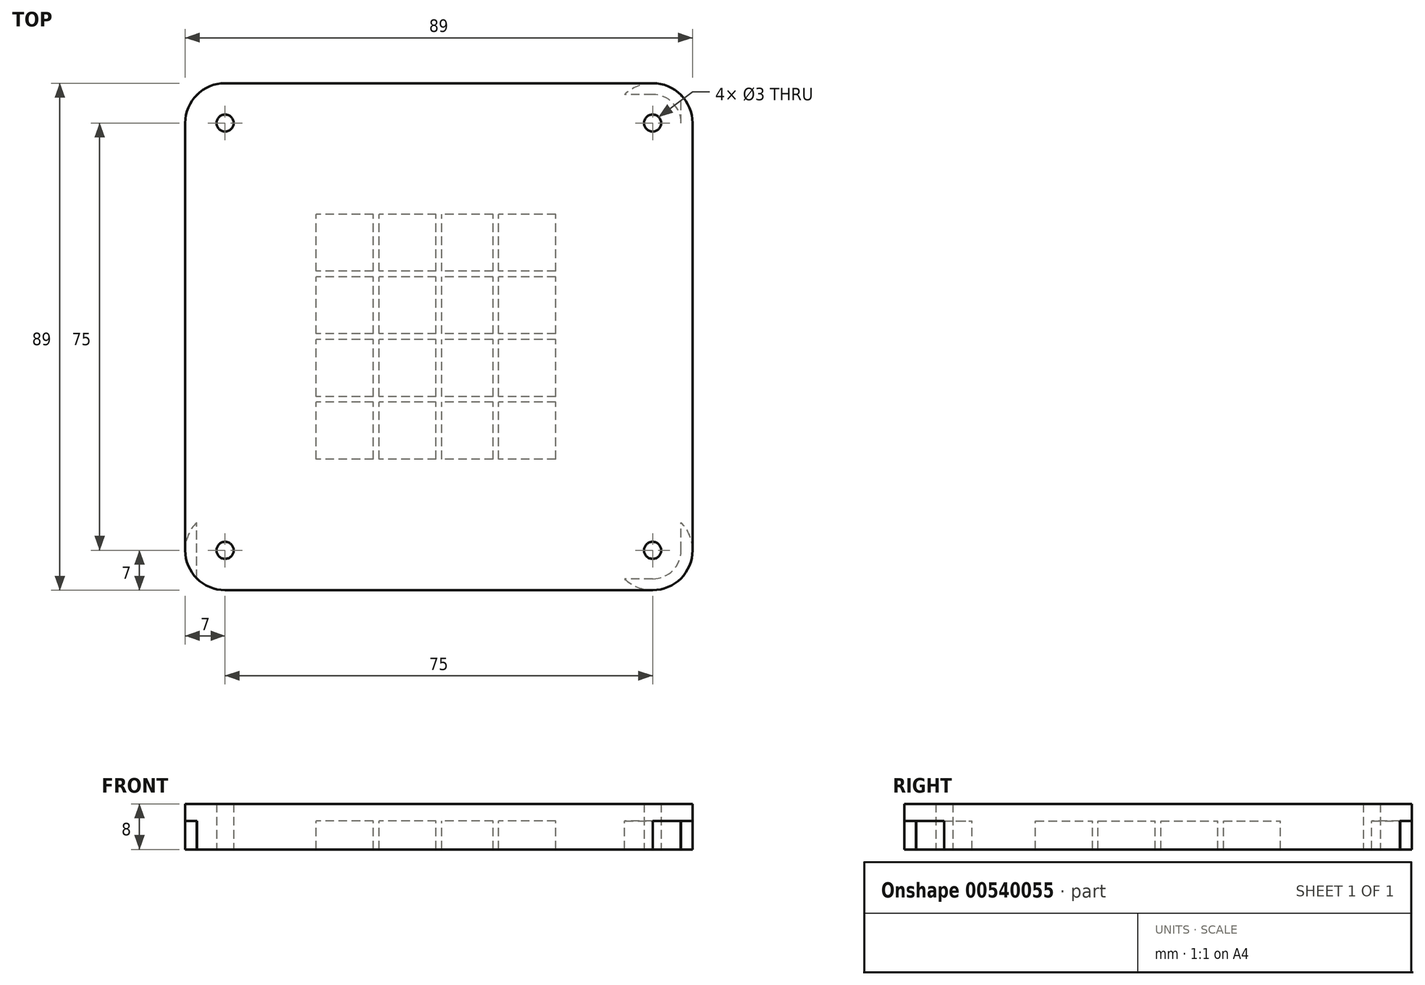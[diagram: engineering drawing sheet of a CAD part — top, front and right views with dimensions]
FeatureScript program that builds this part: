
annotation { "Feature Type Name" : "Feature", "Feature Type Description" : "" }
export const myFeature = defineFeature(function(context is Context, id is Id, definition is map)
    precondition{}
    {
        {
            var Q0;
            Q0=qCreatedBy(makeId("Top.planeOp"),FACE);
            var sketch = newSketch(context, id + "F0", { "sketchPlane" : qUnion([Q0])});
            skLineSegment(sketch, "E0.bottom", {"start": v(37.5, 37.5) * mm, "end": v(-37.5, 37.5) * mm});
            skLineSegment(sketch, "E0.top", {"start": v(37.5, -37.5) * mm, "end": v(-37.5, -37.5) * mm});
            skLineSegment(sketch, "E0.left", {"start": v(37.5, 37.5) * mm, "end": v(37.5, -37.5) * mm});
            skLineSegment(sketch, "E0.right", {"start": v(-37.5, 37.5) * mm, "end": v(-37.5, -37.5) * mm});
            skPoint(sketch, "E0.middle", {"position": v(0, 0) * mm});
            skLineSegment(sketch, "E1.bottom", {"start": v(44.5, 44.5) * mm, "end": v(-44.5, 44.5) * mm});
            skLineSegment(sketch, "E1.top", {"start": v(44.5, -44.5) * mm, "end": v(-44.5, -44.5) * mm});
            skLineSegment(sketch, "E1.left", {"start": v(44.5, 44.5) * mm, "end": v(44.5, -44.5) * mm});
            skLineSegment(sketch, "E1.right", {"start": v(-44.5, 44.5) * mm, "end": v(-44.5, -44.5) * mm});
            skCircle(sketch, "E2", {"center": v(37.5, 37.5) * mm, "radius": 7 * mm});
            skCircle(sketch, "E3", {"center": v(-37.5, 37.5) * mm, "radius": 7 * mm});
            skCircle(sketch, "E4", {"center": v(-37.5, -37.5) * mm, "radius": 7 * mm});
            skCircle(sketch, "E5", {"center": v(37.5, -37.5) * mm, "radius": 7 * mm});
            skCircle(sketch, "E6", {"center": v(-37.5, 37.5) * mm, "radius": 1.5 * mm});
            skCircle(sketch, "E7", {"center": v(37.5, 37.5) * mm, "radius": 1.5 * mm});
            skCircle(sketch, "E8", {"center": v(37.5, -37.5) * mm, "radius": 1.5 * mm});
            skCircle(sketch, "E9", {"center": v(-37.5, -37.5) * mm, "radius": 1.5 * mm});
            skSolve(sketch);
        }
        {
            var Q0;
            {var subQ0=sQuery(id+"F0.wireOp",EDGE,"E2");var subQ1=sQuery(id+"F0.wireOp",EDGE,"E0.bottom");var subQ2=makeQuery(id+"F0.imprint","INTERSECT",VERTEX,{"derivedFrom":[subQ1,subQ0]});Q0=makeQuery(id+"F0.imprint","IMPRINT",FACE,{"disambiguationData":[TD([[makeQuery(id+"F0.imprint","IMPRINT",EDGE,{"disambiguationData":[TD([[subQ2,-1.0]])],"derivedFrom":subQ1}),-1.0]])]});}
            var Q1;
            {var subQ0=sQuery(id+"F0.wireOp",EDGE,"E5");var subQ1=sQuery(id+"F0.wireOp",EDGE,"E0.top");var subQ2=makeQuery(id+"F0.imprint","INTERSECT",VERTEX,{"derivedFrom":[subQ1,subQ0]});Q1=makeQuery(id+"F0.imprint","IMPRINT",FACE,{"disambiguationData":[TD([[makeQuery(id+"F0.imprint","IMPRINT",EDGE,{"disambiguationData":[TD([[subQ2,-1.0]])],"derivedFrom":subQ1}),1.0]])]});}
            var Q2;
            {var subQ0=sQuery(id+"F0.wireOp",EDGE,"E2");var subQ1=sQuery(id+"F0.wireOp",EDGE,"E0.left");var subQ2=makeQuery(id+"F0.imprint","INTERSECT",VERTEX,{"derivedFrom":[subQ1,subQ0]});Q2=makeQuery(id+"F0.imprint","IMPRINT",FACE,{"disambiguationData":[TD([[makeQuery(id+"F0.imprint","IMPRINT",EDGE,{"disambiguationData":[TD([[subQ2,-1.0]])],"derivedFrom":subQ1}),1.0]])]});}
            var Q3;
            {var subQ0=sQuery(id+"F0.wireOp",EDGE,"E3");var subQ1=sQuery(id+"F0.wireOp",EDGE,"E0.right");var subQ2=makeQuery(id+"F0.imprint","INTERSECT",VERTEX,{"derivedFrom":[subQ1,subQ0]});Q3=makeQuery(id+"F0.imprint","IMPRINT",FACE,{"disambiguationData":[TD([[makeQuery(id+"F0.imprint","IMPRINT",EDGE,{"disambiguationData":[TD([[subQ2,-1.0]])],"derivedFrom":subQ1}),-1.0]])]});}
            var Q4;
            {var subQ2=sQuery(id+"F0.wireOp",EDGE,"E0.bottom");var subQ4=sQuery(id+"F0.wireOp",EDGE,"E7");var subQ9=makeQuery(id+"F0.imprint","INTERSECT",VERTEX,{"derivedFrom":[subQ2,subQ4]});Q4=makeQuery(id+"F0.imprint","IMPRINT",FACE,{"disambiguationData":[TD([[makeQuery(id+"F0.imprint","IMPRINT",EDGE,{"disambiguationData":[TD([[subQ9,-1.0]])],"derivedFrom":subQ2}),-1.0]])]});}
            var Q5;
            {var subQ0=sQuery(id+"F0.wireOp",EDGE,"E3");var subQ4=sQuery(id+"F0.wireOp",EDGE,"E0.bottom");var subQ8=makeQuery(id+"F0.imprint","INTERSECT",VERTEX,{"derivedFrom":[subQ4,subQ0]});Q5=makeQuery(id+"F0.imprint","IMPRINT",FACE,{"disambiguationData":[TD([[makeQuery(id+"F0.imprint","IMPRINT",EDGE,{"disambiguationData":[TD([[subQ8,-1.0]])],"derivedFrom":subQ4}),-1.0]])]});}
            var Q6;
            {var subQ4=sQuery(id+"F0.wireOp",EDGE,"E8");var subQ7=sQuery(id+"F0.wireOp",EDGE,"E0.top");var subQ9=makeQuery(id+"F0.imprint","INTERSECT",VERTEX,{"derivedFrom":[subQ7,subQ4]});Q6=makeQuery(id+"F0.imprint","IMPRINT",FACE,{"disambiguationData":[TD([[makeQuery(id+"F0.imprint","IMPRINT",EDGE,{"disambiguationData":[TD([[subQ9,-1.0]])],"derivedFrom":subQ7}),1.0]])]});}
            var Q7;
            {var subQ0=sQuery(id+"F0.wireOp",EDGE,"E4");var subQ5=sQuery(id+"F0.wireOp",EDGE,"E0.top");var subQ6=makeQuery(id+"F0.imprint","INTERSECT",VERTEX,{"derivedFrom":[subQ5,subQ0]});Q7=makeQuery(id+"F0.imprint","IMPRINT",FACE,{"disambiguationData":[TD([[makeQuery(id+"F0.imprint","IMPRINT",EDGE,{"disambiguationData":[TD([[subQ6,-1.0]])],"derivedFrom":subQ5}),1.0]])]});}
            var Q8;
            {var subQ5=sQuery(id+"F0.wireOp",EDGE,"E0.bottom");var subQ7=sQuery(id+"F0.wireOp",EDGE,"E2");var subQ12=makeQuery(id+"F0.imprint","INTERSECT",VERTEX,{"derivedFrom":[subQ5,subQ7]});Q8=makeQuery(id+"F0.imprint","IMPRINT",FACE,{"disambiguationData":[TD([[makeQuery(id+"F0.imprint","IMPRINT",EDGE,{"disambiguationData":[TD([[subQ12,-1.0]])],"derivedFrom":subQ5}),1.0]])]});}
            var Q9;
            {var subQ0=sQuery(id+"F0.wireOp",EDGE,"E3");var subQ1=sQuery(id+"F0.wireOp",EDGE,"E0.bottom");var subQ2=makeQuery(id+"F0.imprint","INTERSECT",VERTEX,{"derivedFrom":[subQ1,subQ0]});Q9=makeQuery(id+"F0.imprint","IMPRINT",FACE,{"disambiguationData":[TD([[makeQuery(id+"F0.imprint","IMPRINT",EDGE,{"disambiguationData":[TD([[subQ2,-1.0]])],"derivedFrom":subQ1}),1.0]])]});}
            var Q10;
            {var subQ0=sQuery(id+"F0.wireOp",EDGE,"E7");var subQ1=sQuery(id+"F0.wireOp",EDGE,"E0.bottom");var subQ2=makeQuery(id+"F0.imprint","INTERSECT",VERTEX,{"derivedFrom":[subQ1,subQ0]});Q10=makeQuery(id+"F0.imprint","IMPRINT",FACE,{"disambiguationData":[TD([[makeQuery(id+"F0.imprint","IMPRINT",EDGE,{"disambiguationData":[TD([[subQ2,-1.0]])],"derivedFrom":subQ1}),1.0]])]});}
            var Q11;
            {var subQ0=sQuery(id+"F0.wireOp",EDGE,"E8");var subQ1=sQuery(id+"F0.wireOp",EDGE,"E0.top");var subQ2=makeQuery(id+"F0.imprint","INTERSECT",VERTEX,{"derivedFrom":[subQ1,subQ0]});Q11=makeQuery(id+"F0.imprint","IMPRINT",FACE,{"disambiguationData":[TD([[makeQuery(id+"F0.imprint","IMPRINT",EDGE,{"disambiguationData":[TD([[subQ2,-1.0]])],"derivedFrom":subQ1}),-1.0]])]});}
            var Q12;
            {var subQ0=sQuery(id+"F0.wireOp",EDGE,"E4");var subQ1=sQuery(id+"F0.wireOp",EDGE,"E0.top");var subQ2=makeQuery(id+"F0.imprint","INTERSECT",VERTEX,{"derivedFrom":[subQ1,subQ0]});Q12=makeQuery(id+"F0.imprint","IMPRINT",FACE,{"disambiguationData":[TD([[makeQuery(id+"F0.imprint","IMPRINT",EDGE,{"disambiguationData":[TD([[subQ2,-1.0]])],"derivedFrom":subQ1}),-1.0]])]});}
            extrude(context, id + "F1", {"entities" : qUnion([Q0, Q1, Q2, Q3, Q4, Q5, Q6, Q7, Q8, Q9, Q10, Q11, Q12]), "depth" : 3 * mm});
        }
        {
            var Q0;
            Q0=makeQuery(id+"F1.opExtrude","CAP_FACE",FACE,{"disambiguationData":[OSD([sQuery(id+"F0.wireOp",EDGE,"E1.bottom"),sQuery(id+"F0.wireOp",EDGE,"E1.top"),sQuery(id+"F0.wireOp",EDGE,"E1.left"),sQuery(id+"F0.wireOp",EDGE,"E1.right"),sQuery(id+"F0.wireOp",EDGE,"E2"),sQuery(id+"F0.wireOp",EDGE,"E3"),sQuery(id+"F0.wireOp",EDGE,"E4"),sQuery(id+"F0.wireOp",EDGE,"E5"),sQuery(id+"F0.wireOp",EDGE,"E6"),sQuery(id+"F0.wireOp",EDGE,"E7"),sQuery(id+"F0.wireOp",EDGE,"E8"),sQuery(id+"F0.wireOp",EDGE,"E9")])],"isStart":true});
            var sketch = newSketch(context, id + "F2", { "sketchPlane" : qUnion([Q0])});
            skLineSegment(sketch, "E10.bottom", {"start": v(42.5, 42.5) * mm, "end": v(-42.5, 42.5) * mm});
            skLineSegment(sketch, "E10.top", {"start": v(42.5, -42.5) * mm, "end": v(-42.5, -42.5) * mm});
            skLineSegment(sketch, "E10.left", {"start": v(42.5, 42.5) * mm, "end": v(42.5, -42.5) * mm});
            skLineSegment(sketch, "E10.right", {"start": v(-42.5, 42.5) * mm, "end": v(-42.5, -42.5) * mm});
            skPoint(sketch, "E10.middle", {"position": v(0, 0) * mm});
            skCircle(sketch, "E11", {"center": v(37.5, 37.5) * mm, "radius": 5 * mm});
            skCircle(sketch, "E12", {"center": v(37.5, 37.5) * mm, "radius": 7 * mm});
            skCircle(sketch, "E13", {"center": v(-37.5, 37.5) * mm, "radius": 5 * mm});
            skCircle(sketch, "E14", {"center": v(-37.5, 37.5) * mm, "radius": 7 * mm});
            skCircle(sketch, "E15", {"center": v(-37.5, -37.5) * mm, "radius": 5 * mm});
            skCircle(sketch, "E16", {"center": v(-37.5, -37.5) * mm, "radius": 7 * mm});
            skCircle(sketch, "E17", {"center": v(37.5, -37.5) * mm, "radius": 5 * mm});
            skCircle(sketch, "E18", {"center": v(37.5, -37.5) * mm, "radius": 7 * mm});
            skLineSegment(sketch, "E19.bottom", {"start": v(0.5, 37.5) * mm, "end": v(-0.5, 37.5) * mm});
            skLineSegment(sketch, "E19.top", {"start": v(0.5, -37.5) * mm, "end": v(-0.5, -37.5) * mm});
            skLineSegment(sketch, "E19.left", {"start": v(0.5, 37.5) * mm, "end": v(0.5, -37.5) * mm});
            skLineSegment(sketch, "E19.right", {"start": v(-0.5, 37.5) * mm, "end": v(-0.5, -37.5) * mm});
            skLineSegment(sketch, "E20.bottom", {"start": v(21.5, 37.5) * mm, "end": v(20.5, 37.5) * mm});
            skLineSegment(sketch, "E20.top", {"start": v(21.5, -37.5) * mm, "end": v(20.5, -37.5) * mm});
            skLineSegment(sketch, "E20.left", {"start": v(21.5, 37.5) * mm, "end": v(21.5, -37.5) * mm});
            skLineSegment(sketch, "E20.right", {"start": v(20.5, 37.5) * mm, "end": v(20.5, -37.5) * mm});
            skPoint(sketch, "E20.middle", {"position": v(21, 0) * mm});
            skLineSegment(sketch, "E21.bottom", {"start": v(-21.5, 37.5) * mm, "end": v(-22.5, 37.5) * mm});
            skLineSegment(sketch, "E21.top", {"start": v(-21.5, -37.5) * mm, "end": v(-22.5, -37.5) * mm});
            skLineSegment(sketch, "E21.left", {"start": v(-21.5, 37.5) * mm, "end": v(-21.5, -37.5) * mm});
            skLineSegment(sketch, "E21.right", {"start": v(-22.5, 37.5) * mm, "end": v(-22.5, -37.5) * mm});
            skPoint(sketch, "E21.middle", {"position": v(-22, 0) * mm});
            skLineSegment(sketch, "E22.bottom", {"start": v(37.5, 0.5) * mm, "end": v(-37.5, 0.5) * mm});
            skLineSegment(sketch, "E22.top", {"start": v(37.5, -0.5) * mm, "end": v(-37.5, -0.5) * mm});
            skLineSegment(sketch, "E22.left", {"start": v(37.5, 0.5) * mm, "end": v(37.5, -0.5) * mm});
            skLineSegment(sketch, "E22.right", {"start": v(-37.5, 0.5) * mm, "end": v(-37.5, -0.5) * mm});
            skLineSegment(sketch, "E23.bottom", {"start": v(37.5, 22.5) * mm, "end": v(-37.5, 22.5) * mm});
            skLineSegment(sketch, "E23.top", {"start": v(37.5, 21.5) * mm, "end": v(-37.5, 21.5) * mm});
            skLineSegment(sketch, "E23.left", {"start": v(37.5, 22.5) * mm, "end": v(37.5, 21.5) * mm});
            skLineSegment(sketch, "E23.right", {"start": v(-37.5, 22.5) * mm, "end": v(-37.5, 21.5) * mm});
            skPoint(sketch, "E23.middle", {"position": v(0, 22) * mm});
            skLineSegment(sketch, "E24.bottom", {"start": v(37.5, -21.5) * mm, "end": v(-37.5, -21.5) * mm});
            skLineSegment(sketch, "E24.top", {"start": v(37.5, -22.5) * mm, "end": v(-37.5, -22.5) * mm});
            skLineSegment(sketch, "E24.left", {"start": v(37.5, -21.5) * mm, "end": v(37.5, -22.5) * mm});
            skLineSegment(sketch, "E24.right", {"start": v(-37.5, -21.5) * mm, "end": v(-37.5, -22.5) * mm});
            skPoint(sketch, "E24.middle", {"position": v(0, -22) * mm});
            skLineSegment(sketch, "E25.bottom", {"start": v(-10.5, 37.5) * mm, "end": v(-11.5, 37.5) * mm});
            skLineSegment(sketch, "E25.top", {"start": v(-10.5, -37.5) * mm, "end": v(-11.5, -37.5) * mm});
            skLineSegment(sketch, "E25.left", {"start": v(-10.5, 37.5) * mm, "end": v(-10.5, -37.5) * mm});
            skLineSegment(sketch, "E25.right", {"start": v(-11.5, 37.5) * mm, "end": v(-11.5, -37.5) * mm});
            skPoint(sketch, "E25.middle", {"position": v(-11, 0) * mm});
            skLineSegment(sketch, "E26.bottom", {"start": v(10.5, 37.5) * mm, "end": v(9.5, 37.5) * mm});
            skLineSegment(sketch, "E26.top", {"start": v(10.5, -37.5) * mm, "end": v(9.5, -37.5) * mm});
            skLineSegment(sketch, "E26.left", {"start": v(10.5, 37.5) * mm, "end": v(10.5, -37.5) * mm});
            skLineSegment(sketch, "E26.right", {"start": v(9.5, 37.5) * mm, "end": v(9.5, -37.5) * mm});
            skPoint(sketch, "E26.middle", {"position": v(10, 0) * mm});
            skLineSegment(sketch, "E27.bottom", {"start": v(37.5, 10.5) * mm, "end": v(-37.5, 10.5) * mm});
            skLineSegment(sketch, "E27.top", {"start": v(37.5, 11.5) * mm, "end": v(-37.5, 11.5) * mm});
            skLineSegment(sketch, "E27.left", {"start": v(37.5, 10.5) * mm, "end": v(37.5, 11.5) * mm});
            skLineSegment(sketch, "E27.right", {"start": v(-37.5, 10.5) * mm, "end": v(-37.5, 11.5) * mm});
            skPoint(sketch, "E27.middle", {"position": v(0, 11) * mm});
            skLineSegment(sketch, "E28.bottom", {"start": v(37.5, -11.5) * mm, "end": v(-37.5, -11.5) * mm});
            skLineSegment(sketch, "E28.top", {"start": v(37.5, -10.5) * mm, "end": v(-37.5, -10.5) * mm});
            skLineSegment(sketch, "E28.left", {"start": v(37.5, -11.5) * mm, "end": v(37.5, -10.5) * mm});
            skLineSegment(sketch, "E28.right", {"start": v(-37.5, -11.5) * mm, "end": v(-37.5, -10.5) * mm});
            skPoint(sketch, "E28.middle", {"position": v(0, -11) * mm});
            skSolve(sketch);
        }
        {
            var Q0;
            {var subQ0=sQuery(id+"F2.wireOp",EDGE,"E10.left");var subQ1=sQuery(id+"F2.wireOp",EDGE,"E10.bottom");var subQ2=makeQuery(id+"F2.imprint","INTERSECT",VERTEX,{"derivedFrom":[subQ1,subQ0]});Q0=makeQuery(id+"F2.imprint","IMPRINT",FACE,{"disambiguationData":[TD([[makeQuery(id+"F2.imprint","IMPRINT",EDGE,{"disambiguationData":[TD([[subQ2,-1.0]])],"derivedFrom":subQ1}),1.0]])]});}
            var Q1;
            {var subQ0=sQuery(id+"F2.wireOp",EDGE,"E10.right");var subQ1=sQuery(id+"F2.wireOp",EDGE,"E10.bottom");var subQ2=makeQuery(id+"F2.imprint","INTERSECT",VERTEX,{"derivedFrom":[subQ1,subQ0]});Q1=makeQuery(id+"F2.imprint","IMPRINT",FACE,{"disambiguationData":[TD([[makeQuery(id+"F2.imprint","IMPRINT",EDGE,{"disambiguationData":[TD([[subQ2,1.0]])],"derivedFrom":subQ1}),1.0]])]});}
            var Q2;
            {var subQ0=sQuery(id+"F2.wireOp",EDGE,"E10.left");var subQ1=sQuery(id+"F2.wireOp",EDGE,"E10.top");var subQ2=makeQuery(id+"F2.imprint","INTERSECT",VERTEX,{"derivedFrom":[subQ1,subQ0]});Q2=makeQuery(id+"F2.imprint","IMPRINT",FACE,{"disambiguationData":[TD([[makeQuery(id+"F2.imprint","IMPRINT",EDGE,{"disambiguationData":[TD([[subQ2,-1.0]])],"derivedFrom":subQ1}),-1.0]])]});}
            var Q3;
            {var subQ0=sQuery(id+"F2.wireOp",EDGE,"E10.right");var subQ1=sQuery(id+"F2.wireOp",EDGE,"E10.top");var subQ2=makeQuery(id+"F2.imprint","INTERSECT",VERTEX,{"derivedFrom":[subQ1,subQ0]});Q3=makeQuery(id+"F2.imprint","IMPRINT",FACE,{"disambiguationData":[TD([[makeQuery(id+"F2.imprint","IMPRINT",EDGE,{"disambiguationData":[TD([[subQ2,1.0]])],"derivedFrom":subQ1}),-1.0]])]});}
            var Q4;
            {var subQ0=sQuery(id+"F2.wireOp",EDGE,"E12");var subQ1=sQuery(id+"F2.wireOp",EDGE,"E10.bottom");var subQ2=makeQuery(id+"F2.imprint","INTERSECT",VERTEX,{"disambiguationData":[OD(0.0)],"derivedFrom":[subQ1,subQ0]});Q4=makeQuery(id+"F2.imprint","IMPRINT",FACE,{"disambiguationData":[TD([[makeQuery(id+"F2.imprint","IMPRINT",EDGE,{"disambiguationData":[TD([[subQ2,-1.0]])],"derivedFrom":subQ1}),-1.0]])]});}
            var Q5;
            {var subQ0=sQuery(id+"F2.wireOp",EDGE,"E14");var subQ1=sQuery(id+"F2.wireOp",EDGE,"E10.bottom");var subQ2=makeQuery(id+"F2.imprint","INTERSECT",VERTEX,{"disambiguationData":[OD(1.0)],"derivedFrom":[subQ1,subQ0]});Q5=makeQuery(id+"F2.imprint","IMPRINT",FACE,{"disambiguationData":[TD([[makeQuery(id+"F2.imprint","IMPRINT",EDGE,{"disambiguationData":[TD([[subQ2,-1.0]])],"derivedFrom":subQ1}),-1.0]])]});}
            var Q6;
            {var subQ0=sQuery(id+"F2.wireOp",EDGE,"E18");var subQ1=sQuery(id+"F2.wireOp",EDGE,"E10.top");var subQ2=makeQuery(id+"F2.imprint","INTERSECT",VERTEX,{"disambiguationData":[OD(0.0)],"derivedFrom":[subQ1,subQ0]});Q6=makeQuery(id+"F2.imprint","IMPRINT",FACE,{"disambiguationData":[TD([[makeQuery(id+"F2.imprint","IMPRINT",EDGE,{"disambiguationData":[TD([[subQ2,-1.0]])],"derivedFrom":subQ1}),1.0]])]});}
            var Q7;
            {var subQ0=sQuery(id+"F2.wireOp",EDGE,"E16");var subQ1=sQuery(id+"F2.wireOp",EDGE,"E10.top");var subQ2=makeQuery(id+"F2.imprint","INTERSECT",VERTEX,{"disambiguationData":[OD(1.0)],"derivedFrom":[subQ1,subQ0]});Q7=makeQuery(id+"F2.imprint","IMPRINT",FACE,{"disambiguationData":[TD([[makeQuery(id+"F2.imprint","IMPRINT",EDGE,{"disambiguationData":[TD([[subQ2,-1.0]])],"derivedFrom":subQ1}),1.0]])]});}
            var Q8;
            {var subQ0=sQuery(id+"F2.wireOp",EDGE,"E12");var subQ1=sQuery(id+"F2.wireOp",EDGE,"E10.left");var subQ2=makeQuery(id+"F2.imprint","INTERSECT",VERTEX,{"disambiguationData":[OD(0.0)],"derivedFrom":[subQ1,subQ0]});Q8=makeQuery(id+"F2.imprint","IMPRINT",FACE,{"disambiguationData":[TD([[makeQuery(id+"F2.imprint","IMPRINT",EDGE,{"disambiguationData":[TD([[subQ2,-1.0]])],"derivedFrom":subQ1}),1.0]])]});}
            var Q9;
            {var subQ0=sQuery(id+"F2.wireOp",EDGE,"E18");var subQ1=sQuery(id+"F2.wireOp",EDGE,"E10.left");var subQ2=makeQuery(id+"F2.imprint","INTERSECT",VERTEX,{"disambiguationData":[OD(1.0)],"derivedFrom":[subQ1,subQ0]});Q9=makeQuery(id+"F2.imprint","IMPRINT",FACE,{"disambiguationData":[TD([[makeQuery(id+"F2.imprint","IMPRINT",EDGE,{"disambiguationData":[TD([[subQ2,-1.0]])],"derivedFrom":subQ1}),1.0]])]});}
            var Q10;
            {var subQ0=sQuery(id+"F2.wireOp",EDGE,"E14");var subQ1=sQuery(id+"F2.wireOp",EDGE,"E10.right");var subQ2=makeQuery(id+"F2.imprint","INTERSECT",VERTEX,{"disambiguationData":[OD(0.0)],"derivedFrom":[subQ1,subQ0]});Q10=makeQuery(id+"F2.imprint","IMPRINT",FACE,{"disambiguationData":[TD([[makeQuery(id+"F2.imprint","IMPRINT",EDGE,{"disambiguationData":[TD([[subQ2,-1.0]])],"derivedFrom":subQ1}),-1.0]])]});}
            var Q11;
            {var subQ0=sQuery(id+"F2.wireOp",EDGE,"E16");var subQ1=sQuery(id+"F2.wireOp",EDGE,"E10.right");var subQ2=makeQuery(id+"F2.imprint","INTERSECT",VERTEX,{"disambiguationData":[OD(1.0)],"derivedFrom":[subQ1,subQ0]});Q11=makeQuery(id+"F2.imprint","IMPRINT",FACE,{"disambiguationData":[TD([[makeQuery(id+"F2.imprint","IMPRINT",EDGE,{"disambiguationData":[TD([[subQ2,-1.0]])],"derivedFrom":subQ1}),-1.0]])]});}
            var Q12;
            {var subQ0=sQuery(id+"F2.wireOp",EDGE,"E12");var subQ1=sQuery(id+"F2.wireOp",EDGE,"E10.bottom");var subQ2=makeQuery(id+"F2.imprint","INTERSECT",VERTEX,{"disambiguationData":[OD(0.0)],"derivedFrom":[subQ1,subQ0]});Q12=makeQuery(id+"F2.imprint","IMPRINT",FACE,{"disambiguationData":[TD([[makeQuery(id+"F2.imprint","IMPRINT",EDGE,{"disambiguationData":[TD([[subQ2,-1.0]])],"derivedFrom":subQ1}),1.0]])]});}
            var Q13;
            {var subQ0=sQuery(id+"F2.wireOp",EDGE,"E11");var subQ1=sQuery(id+"F2.wireOp",EDGE,"E10.bottom");var subQ2=makeQuery(id+"F2.imprint","INTERSECT",VERTEX,{"derivedFrom":[subQ1,subQ0]});Q13=makeQuery(id+"F2.imprint","IMPRINT",FACE,{"disambiguationData":[TD([[makeQuery(id+"F2.imprint","IMPRINT",EDGE,{"disambiguationData":[TD([[subQ2,-1.0]])],"derivedFrom":subQ1}),1.0]])]});}
            var Q14;
            {var subQ0=sQuery(id+"F2.wireOp",EDGE,"E14");var subQ1=sQuery(id+"F2.wireOp",EDGE,"E10.bottom");var subQ2=makeQuery(id+"F2.imprint","INTERSECT",VERTEX,{"disambiguationData":[OD(1.0)],"derivedFrom":[subQ1,subQ0]});Q14=makeQuery(id+"F2.imprint","IMPRINT",FACE,{"disambiguationData":[TD([[makeQuery(id+"F2.imprint","IMPRINT",EDGE,{"disambiguationData":[TD([[subQ2,-1.0]])],"derivedFrom":subQ1}),1.0]])]});}
            var Q15;
            {var subQ0=sQuery(id+"F2.wireOp",EDGE,"E14");var subQ1=sQuery(id+"F2.wireOp",EDGE,"E10.bottom");var subQ2=makeQuery(id+"F2.imprint","INTERSECT",VERTEX,{"disambiguationData":[OD(0.0)],"derivedFrom":[subQ1,subQ0]});Q15=makeQuery(id+"F2.imprint","IMPRINT",FACE,{"disambiguationData":[TD([[makeQuery(id+"F2.imprint","IMPRINT",EDGE,{"disambiguationData":[TD([[subQ2,1.0]])],"derivedFrom":subQ1}),1.0]])]});}
            var Q16;
            {var subQ0=sQuery(id+"F2.wireOp",EDGE,"E18");var subQ1=sQuery(id+"F2.wireOp",EDGE,"E10.top");var subQ2=makeQuery(id+"F2.imprint","INTERSECT",VERTEX,{"disambiguationData":[OD(0.0)],"derivedFrom":[subQ1,subQ0]});Q16=makeQuery(id+"F2.imprint","IMPRINT",FACE,{"disambiguationData":[TD([[makeQuery(id+"F2.imprint","IMPRINT",EDGE,{"disambiguationData":[TD([[subQ2,-1.0]])],"derivedFrom":subQ1}),-1.0]])]});}
            var Q17;
            {var subQ0=sQuery(id+"F2.wireOp",EDGE,"E17");var subQ1=sQuery(id+"F2.wireOp",EDGE,"E10.top");var subQ2=makeQuery(id+"F2.imprint","INTERSECT",VERTEX,{"derivedFrom":[subQ1,subQ0]});Q17=makeQuery(id+"F2.imprint","IMPRINT",FACE,{"disambiguationData":[TD([[makeQuery(id+"F2.imprint","IMPRINT",EDGE,{"disambiguationData":[TD([[subQ2,-1.0]])],"derivedFrom":subQ1}),-1.0]])]});}
            var Q18;
            {var subQ0=sQuery(id+"F2.wireOp",EDGE,"E16");var subQ1=sQuery(id+"F2.wireOp",EDGE,"E10.top");var subQ2=makeQuery(id+"F2.imprint","INTERSECT",VERTEX,{"disambiguationData":[OD(1.0)],"derivedFrom":[subQ1,subQ0]});Q18=makeQuery(id+"F2.imprint","IMPRINT",FACE,{"disambiguationData":[TD([[makeQuery(id+"F2.imprint","IMPRINT",EDGE,{"disambiguationData":[TD([[subQ2,-1.0]])],"derivedFrom":subQ1}),-1.0]])]});}
            var Q19;
            {var subQ0=sQuery(id+"F2.wireOp",EDGE,"E16");var subQ1=sQuery(id+"F2.wireOp",EDGE,"E10.top");var subQ2=makeQuery(id+"F2.imprint","INTERSECT",VERTEX,{"disambiguationData":[OD(0.0)],"derivedFrom":[subQ1,subQ0]});Q19=makeQuery(id+"F2.imprint","IMPRINT",FACE,{"disambiguationData":[TD([[makeQuery(id+"F2.imprint","IMPRINT",EDGE,{"disambiguationData":[TD([[subQ2,1.0]])],"derivedFrom":subQ1}),-1.0]])]});}
            var Q20;
            {var subQ5=makeQuery(id+"F1.opExtrude","CAP_EDGE",EDGE,{"disambiguationData":[OSD([sQuery(id+"F0.wireOp",EDGE,"E1.top")])],"isStart":true});Q20=makeQuery(id+"F2.imprint","IMPRINT",FACE,{"disambiguationData":[TD([[makeQuery(id+"F2.imprint","IMPRINT",EDGE,{"derivedFrom":subQ5}),1.0]])]});}
            var Q21;
            {var subQ5=makeQuery(id+"F1.opExtrude","CAP_EDGE",EDGE,{"disambiguationData":[OSD([sQuery(id+"F0.wireOp",EDGE,"E1.right")])],"isStart":true});Q21=makeQuery(id+"F2.imprint","IMPRINT",FACE,{"disambiguationData":[TD([[makeQuery(id+"F2.imprint","IMPRINT",EDGE,{"derivedFrom":subQ5}),-1.0]])]});}
            var Q22;
            {var subQ5=makeQuery(id+"F1.opExtrude","CAP_EDGE",EDGE,{"disambiguationData":[OSD([sQuery(id+"F0.wireOp",EDGE,"E1.left")])],"isStart":true});Q22=makeQuery(id+"F2.imprint","IMPRINT",FACE,{"disambiguationData":[TD([[makeQuery(id+"F2.imprint","IMPRINT",EDGE,{"derivedFrom":subQ5}),1.0]])]});}
            var Q23;
            {var subQ5=makeQuery(id+"F1.opExtrude","CAP_EDGE",EDGE,{"disambiguationData":[OSD([sQuery(id+"F0.wireOp",EDGE,"E1.bottom")])],"isStart":true});Q23=makeQuery(id+"F2.imprint","IMPRINT",FACE,{"disambiguationData":[TD([[makeQuery(id+"F2.imprint","IMPRINT",EDGE,{"derivedFrom":subQ5}),-1.0]])]});}
            var Q24;
            {var subQ0=sQuery(id+"F2.wireOp",EDGE,"E19.bottom");Q24=makeQuery(id+"F2.imprint","IMPRINT",FACE,{"disambiguationData":[TD([[makeQuery(id+"F2.imprint","IMPRINT",EDGE,{"derivedFrom":subQ0}),1.0]])]});}
            var Q25;
            {var subQ0=sQuery(id+"F2.wireOp",EDGE,"E21.bottom");Q25=makeQuery(id+"F2.imprint","IMPRINT",FACE,{"disambiguationData":[TD([[makeQuery(id+"F2.imprint","IMPRINT",EDGE,{"derivedFrom":subQ0}),1.0]])]});}
            var Q26;
            {var subQ0=sQuery(id+"F2.wireOp",EDGE,"E23.bottom");var subQ1=sQuery(id+"F2.wireOp",EDGE,"E19.right");var subQ2=makeQuery(id+"F2.imprint","INTERSECT",VERTEX,{"derivedFrom":[subQ1,subQ0]});Q26=makeQuery(id+"F2.imprint","IMPRINT",FACE,{"disambiguationData":[TD([[makeQuery(id+"F2.imprint","IMPRINT",EDGE,{"disambiguationData":[TD([[subQ2,-1.0]])],"derivedFrom":subQ1}),-1.0]])]});}
            var Q27;
            {var subQ5=sQuery(id+"F2.wireOp",EDGE,"E23.right");Q27=makeQuery(id+"F2.imprint","IMPRINT",FACE,{"disambiguationData":[TD([[makeQuery(id+"F2.imprint","IMPRINT",EDGE,{"derivedFrom":subQ5}),1.0]])]});}
            var Q28;
            {var subQ5=sQuery(id+"F2.wireOp",EDGE,"E22.right");Q28=makeQuery(id+"F2.imprint","IMPRINT",FACE,{"disambiguationData":[TD([[makeQuery(id+"F2.imprint","IMPRINT",EDGE,{"derivedFrom":subQ5}),1.0]])]});}
            var Q29;
            {var subQ0=sQuery(id+"F2.wireOp",EDGE,"E22.bottom");var subQ1=sQuery(id+"F2.wireOp",EDGE,"E19.right");var subQ2=makeQuery(id+"F2.imprint","INTERSECT",VERTEX,{"derivedFrom":[subQ1,subQ0]});Q29=makeQuery(id+"F2.imprint","IMPRINT",FACE,{"disambiguationData":[TD([[makeQuery(id+"F2.imprint","IMPRINT",EDGE,{"disambiguationData":[TD([[subQ2,-1.0]])],"derivedFrom":subQ1}),-1.0]])]});}
            var Q30;
            {var subQ0=sQuery(id+"F2.wireOp",EDGE,"E22.top");var subQ1=sQuery(id+"F2.wireOp",EDGE,"E21.left");var subQ2=makeQuery(id+"F2.imprint","INTERSECT",VERTEX,{"derivedFrom":[subQ1,subQ0]});Q30=makeQuery(id+"F2.imprint","IMPRINT",FACE,{"disambiguationData":[TD([[makeQuery(id+"F2.imprint","IMPRINT",EDGE,{"disambiguationData":[TD([[subQ2,-1.0]])],"derivedFrom":subQ1}),-1.0]])]});}
            var Q31;
            {var subQ0=sQuery(id+"F2.wireOp",EDGE,"E22.top");var subQ1=sQuery(id+"F2.wireOp",EDGE,"E19.left");var subQ2=makeQuery(id+"F2.imprint","INTERSECT",VERTEX,{"derivedFrom":[subQ1,subQ0]});Q31=makeQuery(id+"F2.imprint","IMPRINT",FACE,{"disambiguationData":[TD([[makeQuery(id+"F2.imprint","IMPRINT",EDGE,{"disambiguationData":[TD([[subQ2,-1.0]])],"derivedFrom":subQ1}),-1.0]])]});}
            var Q32;
            {var subQ0=sQuery(id+"F2.wireOp",EDGE,"E22.top");var subQ1=sQuery(id+"F2.wireOp",EDGE,"E20.left");var subQ2=makeQuery(id+"F2.imprint","INTERSECT",VERTEX,{"derivedFrom":[subQ1,subQ0]});Q32=makeQuery(id+"F2.imprint","IMPRINT",FACE,{"disambiguationData":[TD([[makeQuery(id+"F2.imprint","IMPRINT",EDGE,{"disambiguationData":[TD([[subQ2,-1.0]])],"derivedFrom":subQ1}),-1.0]])]});}
            var Q33;
            {var subQ0=sQuery(id+"F2.wireOp",EDGE,"E23.bottom");var subQ1=sQuery(id+"F2.wireOp",EDGE,"E19.left");var subQ2=makeQuery(id+"F2.imprint","INTERSECT",VERTEX,{"derivedFrom":[subQ1,subQ0]});Q33=makeQuery(id+"F2.imprint","IMPRINT",FACE,{"disambiguationData":[TD([[makeQuery(id+"F2.imprint","IMPRINT",EDGE,{"disambiguationData":[TD([[subQ2,-1.0]])],"derivedFrom":subQ1}),1.0]])]});}
            var Q34;
            {var subQ0=sQuery(id+"F2.wireOp",EDGE,"E22.bottom");var subQ1=sQuery(id+"F2.wireOp",EDGE,"E19.left");var subQ2=makeQuery(id+"F2.imprint","INTERSECT",VERTEX,{"derivedFrom":[subQ1,subQ0]});Q34=makeQuery(id+"F2.imprint","IMPRINT",FACE,{"disambiguationData":[TD([[makeQuery(id+"F2.imprint","IMPRINT",EDGE,{"disambiguationData":[TD([[subQ2,-1.0]])],"derivedFrom":subQ1}),1.0]])]});}
            var Q35;
            {var subQ0=sQuery(id+"F2.wireOp",EDGE,"E24.bottom");var subQ1=sQuery(id+"F2.wireOp",EDGE,"E19.left");var subQ2=makeQuery(id+"F2.imprint","INTERSECT",VERTEX,{"derivedFrom":[subQ1,subQ0]});Q35=makeQuery(id+"F2.imprint","IMPRINT",FACE,{"disambiguationData":[TD([[makeQuery(id+"F2.imprint","IMPRINT",EDGE,{"disambiguationData":[TD([[subQ2,-1.0]])],"derivedFrom":subQ1}),1.0]])]});}
            var Q36;
            {var subQ0=sQuery(id+"F2.wireOp",EDGE,"E24.bottom");var subQ1=sQuery(id+"F2.wireOp",EDGE,"E19.right");var subQ2=makeQuery(id+"F2.imprint","INTERSECT",VERTEX,{"derivedFrom":[subQ1,subQ0]});Q36=makeQuery(id+"F2.imprint","IMPRINT",FACE,{"disambiguationData":[TD([[makeQuery(id+"F2.imprint","IMPRINT",EDGE,{"disambiguationData":[TD([[subQ2,-1.0]])],"derivedFrom":subQ1}),-1.0]])]});}
            var Q37;
            {var subQ0=sQuery(id+"F2.wireOp",EDGE,"E20.bottom");Q37=makeQuery(id+"F2.imprint","IMPRINT",FACE,{"disambiguationData":[TD([[makeQuery(id+"F2.imprint","IMPRINT",EDGE,{"derivedFrom":subQ0}),1.0]])]});}
            var Q38;
            {var subQ5=sQuery(id+"F2.wireOp",EDGE,"E22.left");Q38=makeQuery(id+"F2.imprint","IMPRINT",FACE,{"disambiguationData":[TD([[makeQuery(id+"F2.imprint","IMPRINT",EDGE,{"derivedFrom":subQ5}),-1.0]])]});}
            var Q39;
            {var subQ5=sQuery(id+"F2.wireOp",EDGE,"E24.left");Q39=makeQuery(id+"F2.imprint","IMPRINT",FACE,{"disambiguationData":[TD([[makeQuery(id+"F2.imprint","IMPRINT",EDGE,{"derivedFrom":subQ5}),-1.0]])]});}
            var Q40;
            {var subQ0=sQuery(id+"F2.wireOp",EDGE,"E20.top");Q40=makeQuery(id+"F2.imprint","IMPRINT",FACE,{"disambiguationData":[TD([[makeQuery(id+"F2.imprint","IMPRINT",EDGE,{"derivedFrom":subQ0}),-1.0]])]});}
            var Q41;
            {var subQ0=sQuery(id+"F2.wireOp",EDGE,"E19.top");Q41=makeQuery(id+"F2.imprint","IMPRINT",FACE,{"disambiguationData":[TD([[makeQuery(id+"F2.imprint","IMPRINT",EDGE,{"derivedFrom":subQ0}),-1.0]])]});}
            var Q42;
            {var subQ0=sQuery(id+"F2.wireOp",EDGE,"E21.top");Q42=makeQuery(id+"F2.imprint","IMPRINT",FACE,{"disambiguationData":[TD([[makeQuery(id+"F2.imprint","IMPRINT",EDGE,{"derivedFrom":subQ0}),-1.0]])]});}
            var Q43;
            {var subQ5=sQuery(id+"F2.wireOp",EDGE,"E24.right");Q43=makeQuery(id+"F2.imprint","IMPRINT",FACE,{"disambiguationData":[TD([[makeQuery(id+"F2.imprint","IMPRINT",EDGE,{"derivedFrom":subQ5}),1.0]])]});}
            var Q44;
            {var subQ5=sQuery(id+"F2.wireOp",EDGE,"E23.left");Q44=makeQuery(id+"F2.imprint","IMPRINT",FACE,{"disambiguationData":[TD([[makeQuery(id+"F2.imprint","IMPRINT",EDGE,{"derivedFrom":subQ5}),-1.0]])]});}
            var Q45;
            {var subQ0=sQuery(id+"F2.wireOp",EDGE,"E23.top");var subQ1=sQuery(id+"F2.wireOp",EDGE,"E20.left");var subQ2=makeQuery(id+"F2.imprint","INTERSECT",VERTEX,{"derivedFrom":[subQ1,subQ0]});Q45=makeQuery(id+"F2.imprint","IMPRINT",FACE,{"disambiguationData":[TD([[makeQuery(id+"F2.imprint","IMPRINT",EDGE,{"disambiguationData":[TD([[subQ2,-1.0]])],"derivedFrom":subQ1}),-1.0]])]});}
            var Q46;
            {var subQ0=sQuery(id+"F2.wireOp",EDGE,"E23.top");var subQ1=sQuery(id+"F2.wireOp",EDGE,"E19.left");var subQ2=makeQuery(id+"F2.imprint","INTERSECT",VERTEX,{"derivedFrom":[subQ1,subQ0]});Q46=makeQuery(id+"F2.imprint","IMPRINT",FACE,{"disambiguationData":[TD([[makeQuery(id+"F2.imprint","IMPRINT",EDGE,{"disambiguationData":[TD([[subQ2,-1.0]])],"derivedFrom":subQ1}),-1.0]])]});}
            var Q47;
            {var subQ0=sQuery(id+"F2.wireOp",EDGE,"E23.top");var subQ1=sQuery(id+"F2.wireOp",EDGE,"E21.left");var subQ2=makeQuery(id+"F2.imprint","INTERSECT",VERTEX,{"derivedFrom":[subQ1,subQ0]});Q47=makeQuery(id+"F2.imprint","IMPRINT",FACE,{"disambiguationData":[TD([[makeQuery(id+"F2.imprint","IMPRINT",EDGE,{"disambiguationData":[TD([[subQ2,-1.0]])],"derivedFrom":subQ1}),-1.0]])]});}
            var Q48;
            {var subQ0=sQuery(id+"F2.wireOp",EDGE,"E23.bottom");var subQ1=sQuery(id+"F2.wireOp",EDGE,"E19.left");var subQ2=makeQuery(id+"F2.imprint","INTERSECT",VERTEX,{"derivedFrom":[subQ1,subQ0]});Q48=makeQuery(id+"F2.imprint","IMPRINT",FACE,{"disambiguationData":[TD([[makeQuery(id+"F2.imprint","IMPRINT",EDGE,{"disambiguationData":[TD([[subQ2,-1.0]])],"derivedFrom":subQ1}),-1.0]])]});}
            var Q49;
            {var subQ0=sQuery(id+"F2.wireOp",EDGE,"E23.bottom");var subQ1=sQuery(id+"F2.wireOp",EDGE,"E20.left");var subQ2=makeQuery(id+"F2.imprint","INTERSECT",VERTEX,{"derivedFrom":[subQ1,subQ0]});Q49=makeQuery(id+"F2.imprint","IMPRINT",FACE,{"disambiguationData":[TD([[makeQuery(id+"F2.imprint","IMPRINT",EDGE,{"disambiguationData":[TD([[subQ2,-1.0]])],"derivedFrom":subQ1}),-1.0]])]});}
            var Q50;
            {var subQ0=sQuery(id+"F2.wireOp",EDGE,"E23.bottom");var subQ1=sQuery(id+"F2.wireOp",EDGE,"E21.left");var subQ2=makeQuery(id+"F2.imprint","INTERSECT",VERTEX,{"derivedFrom":[subQ1,subQ0]});Q50=makeQuery(id+"F2.imprint","IMPRINT",FACE,{"disambiguationData":[TD([[makeQuery(id+"F2.imprint","IMPRINT",EDGE,{"disambiguationData":[TD([[subQ2,-1.0]])],"derivedFrom":subQ1}),-1.0]])]});}
            var Q51;
            {var subQ0=sQuery(id+"F2.wireOp",EDGE,"E22.bottom");var subQ1=sQuery(id+"F2.wireOp",EDGE,"E21.left");var subQ2=makeQuery(id+"F2.imprint","INTERSECT",VERTEX,{"derivedFrom":[subQ1,subQ0]});Q51=makeQuery(id+"F2.imprint","IMPRINT",FACE,{"disambiguationData":[TD([[makeQuery(id+"F2.imprint","IMPRINT",EDGE,{"disambiguationData":[TD([[subQ2,-1.0]])],"derivedFrom":subQ1}),-1.0]])]});}
            var Q52;
            {var subQ0=sQuery(id+"F2.wireOp",EDGE,"E22.bottom");var subQ1=sQuery(id+"F2.wireOp",EDGE,"E19.left");var subQ2=makeQuery(id+"F2.imprint","INTERSECT",VERTEX,{"derivedFrom":[subQ1,subQ0]});Q52=makeQuery(id+"F2.imprint","IMPRINT",FACE,{"disambiguationData":[TD([[makeQuery(id+"F2.imprint","IMPRINT",EDGE,{"disambiguationData":[TD([[subQ2,-1.0]])],"derivedFrom":subQ1}),-1.0]])]});}
            var Q53;
            {var subQ0=sQuery(id+"F2.wireOp",EDGE,"E22.bottom");var subQ1=sQuery(id+"F2.wireOp",EDGE,"E20.left");var subQ2=makeQuery(id+"F2.imprint","INTERSECT",VERTEX,{"derivedFrom":[subQ1,subQ0]});Q53=makeQuery(id+"F2.imprint","IMPRINT",FACE,{"disambiguationData":[TD([[makeQuery(id+"F2.imprint","IMPRINT",EDGE,{"disambiguationData":[TD([[subQ2,-1.0]])],"derivedFrom":subQ1}),-1.0]])]});}
            var Q54;
            {var subQ0=sQuery(id+"F2.wireOp",EDGE,"E24.bottom");var subQ1=sQuery(id+"F2.wireOp",EDGE,"E20.left");var subQ2=makeQuery(id+"F2.imprint","INTERSECT",VERTEX,{"derivedFrom":[subQ1,subQ0]});Q54=makeQuery(id+"F2.imprint","IMPRINT",FACE,{"disambiguationData":[TD([[makeQuery(id+"F2.imprint","IMPRINT",EDGE,{"disambiguationData":[TD([[subQ2,-1.0]])],"derivedFrom":subQ1}),-1.0]])]});}
            var Q55;
            {var subQ0=sQuery(id+"F2.wireOp",EDGE,"E24.bottom");var subQ1=sQuery(id+"F2.wireOp",EDGE,"E19.left");var subQ2=makeQuery(id+"F2.imprint","INTERSECT",VERTEX,{"derivedFrom":[subQ1,subQ0]});Q55=makeQuery(id+"F2.imprint","IMPRINT",FACE,{"disambiguationData":[TD([[makeQuery(id+"F2.imprint","IMPRINT",EDGE,{"disambiguationData":[TD([[subQ2,-1.0]])],"derivedFrom":subQ1}),-1.0]])]});}
            var Q56;
            {var subQ0=sQuery(id+"F2.wireOp",EDGE,"E24.bottom");var subQ1=sQuery(id+"F2.wireOp",EDGE,"E21.left");var subQ2=makeQuery(id+"F2.imprint","INTERSECT",VERTEX,{"derivedFrom":[subQ1,subQ0]});Q56=makeQuery(id+"F2.imprint","IMPRINT",FACE,{"disambiguationData":[TD([[makeQuery(id+"F2.imprint","IMPRINT",EDGE,{"disambiguationData":[TD([[subQ2,-1.0]])],"derivedFrom":subQ1}),-1.0]])]});}
            var Q57;
            {var subQ5=sQuery(id+"F2.wireOp",EDGE,"E25.bottom");Q57=makeQuery(id+"F2.imprint","IMPRINT",FACE,{"disambiguationData":[TD([[makeQuery(id+"F2.imprint","IMPRINT",EDGE,{"derivedFrom":subQ5}),1.0]])]});}
            var Q58;
            {var subQ0=sQuery(id+"F2.wireOp",EDGE,"E23.bottom");var subQ1=sQuery(id+"F2.wireOp",EDGE,"E21.left");var subQ2=makeQuery(id+"F2.imprint","INTERSECT",VERTEX,{"derivedFrom":[subQ1,subQ0]});Q58=makeQuery(id+"F2.imprint","IMPRINT",FACE,{"disambiguationData":[TD([[makeQuery(id+"F2.imprint","IMPRINT",EDGE,{"disambiguationData":[TD([[subQ2,-1.0]])],"derivedFrom":subQ1}),1.0]])]});}
            var Q59;
            {var subQ0=sQuery(id+"F2.wireOp",EDGE,"E25.left");var subQ1=sQuery(id+"F2.wireOp",EDGE,"E23.top");var subQ2=makeQuery(id+"F2.imprint","INTERSECT",VERTEX,{"derivedFrom":[subQ1,subQ0]});Q59=makeQuery(id+"F2.imprint","IMPRINT",FACE,{"disambiguationData":[TD([[makeQuery(id+"F2.imprint","IMPRINT",EDGE,{"disambiguationData":[TD([[subQ2,-1.0]])],"derivedFrom":subQ1}),1.0]])]});}
            var Q60;
            {var subQ5=sQuery(id+"F2.wireOp",EDGE,"E27.right");Q60=makeQuery(id+"F2.imprint","IMPRINT",FACE,{"disambiguationData":[TD([[makeQuery(id+"F2.imprint","IMPRINT",EDGE,{"derivedFrom":subQ5}),-1.0]])]});}
            var Q61;
            {var subQ0=sQuery(id+"F2.wireOp",EDGE,"E27.top");var subQ1=sQuery(id+"F2.wireOp",EDGE,"E21.left");var subQ2=makeQuery(id+"F2.imprint","INTERSECT",VERTEX,{"derivedFrom":[subQ1,subQ0]});Q61=makeQuery(id+"F2.imprint","IMPRINT",FACE,{"disambiguationData":[TD([[makeQuery(id+"F2.imprint","IMPRINT",EDGE,{"disambiguationData":[TD([[subQ2,-1.0]])],"derivedFrom":subQ1}),-1.0]])]});}
            var Q62;
            {var subQ0=sQuery(id+"F2.wireOp",EDGE,"E27.bottom");var subQ1=sQuery(id+"F2.wireOp",EDGE,"E21.left");var subQ2=makeQuery(id+"F2.imprint","INTERSECT",VERTEX,{"derivedFrom":[subQ1,subQ0]});Q62=makeQuery(id+"F2.imprint","IMPRINT",FACE,{"disambiguationData":[TD([[makeQuery(id+"F2.imprint","IMPRINT",EDGE,{"disambiguationData":[TD([[subQ2,-1.0]])],"derivedFrom":subQ1}),-1.0]])]});}
            var Q63;
            {var subQ0=sQuery(id+"F2.wireOp",EDGE,"E27.top");var subQ1=sQuery(id+"F2.wireOp",EDGE,"E21.left");var subQ2=makeQuery(id+"F2.imprint","INTERSECT",VERTEX,{"derivedFrom":[subQ1,subQ0]});Q63=makeQuery(id+"F2.imprint","IMPRINT",FACE,{"disambiguationData":[TD([[makeQuery(id+"F2.imprint","IMPRINT",EDGE,{"disambiguationData":[TD([[subQ2,-1.0]])],"derivedFrom":subQ1}),1.0]])]});}
            var Q64;
            {var subQ0=sQuery(id+"F2.wireOp",EDGE,"E25.left");var subQ1=sQuery(id+"F2.wireOp",EDGE,"E22.bottom");var subQ2=makeQuery(id+"F2.imprint","INTERSECT",VERTEX,{"derivedFrom":[subQ1,subQ0]});Q64=makeQuery(id+"F2.imprint","IMPRINT",FACE,{"disambiguationData":[TD([[makeQuery(id+"F2.imprint","IMPRINT",EDGE,{"disambiguationData":[TD([[subQ2,-1.0]])],"derivedFrom":subQ1}),-1.0]])]});}
            var Q65;
            {var subQ0=sQuery(id+"F2.wireOp",EDGE,"E27.top");var subQ1=sQuery(id+"F2.wireOp",EDGE,"E25.left");var subQ2=makeQuery(id+"F2.imprint","INTERSECT",VERTEX,{"derivedFrom":[subQ1,subQ0]});Q65=makeQuery(id+"F2.imprint","IMPRINT",FACE,{"disambiguationData":[TD([[makeQuery(id+"F2.imprint","IMPRINT",EDGE,{"disambiguationData":[TD([[subQ2,-1.0]])],"derivedFrom":subQ1}),-1.0]])]});}
            var Q66;
            {var subQ0=sQuery(id+"F2.wireOp",EDGE,"E27.bottom");var subQ1=sQuery(id+"F2.wireOp",EDGE,"E19.left");var subQ2=makeQuery(id+"F2.imprint","INTERSECT",VERTEX,{"derivedFrom":[subQ1,subQ0]});Q66=makeQuery(id+"F2.imprint","IMPRINT",FACE,{"disambiguationData":[TD([[makeQuery(id+"F2.imprint","IMPRINT",EDGE,{"disambiguationData":[TD([[subQ2,-1.0]])],"derivedFrom":subQ1}),-1.0]])]});}
            var Q67;
            {var subQ0=sQuery(id+"F2.wireOp",EDGE,"E27.top");var subQ1=sQuery(id+"F2.wireOp",EDGE,"E19.left");var subQ2=makeQuery(id+"F2.imprint","INTERSECT",VERTEX,{"derivedFrom":[subQ1,subQ0]});Q67=makeQuery(id+"F2.imprint","IMPRINT",FACE,{"disambiguationData":[TD([[makeQuery(id+"F2.imprint","IMPRINT",EDGE,{"disambiguationData":[TD([[subQ2,-1.0]])],"derivedFrom":subQ1}),1.0]])]});}
            var Q68;
            {var subQ0=sQuery(id+"F2.wireOp",EDGE,"E26.left");var subQ1=sQuery(id+"F2.wireOp",EDGE,"E22.bottom");var subQ2=makeQuery(id+"F2.imprint","INTERSECT",VERTEX,{"derivedFrom":[subQ1,subQ0]});Q68=makeQuery(id+"F2.imprint","IMPRINT",FACE,{"disambiguationData":[TD([[makeQuery(id+"F2.imprint","IMPRINT",EDGE,{"disambiguationData":[TD([[subQ2,-1.0]])],"derivedFrom":subQ1}),-1.0]])]});}
            var Q69;
            {var subQ0=sQuery(id+"F2.wireOp",EDGE,"E27.top");var subQ1=sQuery(id+"F2.wireOp",EDGE,"E20.right");var subQ2=makeQuery(id+"F2.imprint","INTERSECT",VERTEX,{"derivedFrom":[subQ1,subQ0]});Q69=makeQuery(id+"F2.imprint","IMPRINT",FACE,{"disambiguationData":[TD([[makeQuery(id+"F2.imprint","IMPRINT",EDGE,{"disambiguationData":[TD([[subQ2,-1.0]])],"derivedFrom":subQ1}),-1.0]])]});}
            var Q70;
            {var subQ5=sQuery(id+"F2.wireOp",EDGE,"E26.bottom");Q70=makeQuery(id+"F2.imprint","IMPRINT",FACE,{"disambiguationData":[TD([[makeQuery(id+"F2.imprint","IMPRINT",EDGE,{"derivedFrom":subQ5}),1.0]])]});}
            var Q71;
            {var subQ0=sQuery(id+"F2.wireOp",EDGE,"E26.left");var subQ1=sQuery(id+"F2.wireOp",EDGE,"E23.bottom");var subQ2=makeQuery(id+"F2.imprint","INTERSECT",VERTEX,{"derivedFrom":[subQ1,subQ0]});Q71=makeQuery(id+"F2.imprint","IMPRINT",FACE,{"disambiguationData":[TD([[makeQuery(id+"F2.imprint","IMPRINT",EDGE,{"disambiguationData":[TD([[subQ2,-1.0]])],"derivedFrom":subQ1}),1.0]])]});}
            var Q72;
            {var subQ0=sQuery(id+"F2.wireOp",EDGE,"E23.bottom");var subQ1=sQuery(id+"F2.wireOp",EDGE,"E20.right");var subQ2=makeQuery(id+"F2.imprint","INTERSECT",VERTEX,{"derivedFrom":[subQ1,subQ0]});Q72=makeQuery(id+"F2.imprint","IMPRINT",FACE,{"disambiguationData":[TD([[makeQuery(id+"F2.imprint","IMPRINT",EDGE,{"disambiguationData":[TD([[subQ2,-1.0]])],"derivedFrom":subQ1}),-1.0]])]});}
            var Q73;
            {var subQ0=sQuery(id+"F2.wireOp",EDGE,"E26.left");var subQ1=sQuery(id+"F2.wireOp",EDGE,"E23.top");var subQ2=makeQuery(id+"F2.imprint","INTERSECT",VERTEX,{"derivedFrom":[subQ1,subQ0]});Q73=makeQuery(id+"F2.imprint","IMPRINT",FACE,{"disambiguationData":[TD([[makeQuery(id+"F2.imprint","IMPRINT",EDGE,{"disambiguationData":[TD([[subQ2,-1.0]])],"derivedFrom":subQ1}),1.0]])]});}
            var Q74;
            {var subQ5=sQuery(id+"F2.wireOp",EDGE,"E27.left");Q74=makeQuery(id+"F2.imprint","IMPRINT",FACE,{"disambiguationData":[TD([[makeQuery(id+"F2.imprint","IMPRINT",EDGE,{"derivedFrom":subQ5}),1.0]])]});}
            var Q75;
            {var subQ0=sQuery(id+"F2.wireOp",EDGE,"E27.bottom");var subQ1=sQuery(id+"F2.wireOp",EDGE,"E20.left");var subQ2=makeQuery(id+"F2.imprint","INTERSECT",VERTEX,{"derivedFrom":[subQ1,subQ0]});Q75=makeQuery(id+"F2.imprint","IMPRINT",FACE,{"disambiguationData":[TD([[makeQuery(id+"F2.imprint","IMPRINT",EDGE,{"disambiguationData":[TD([[subQ2,-1.0]])],"derivedFrom":subQ1}),-1.0]])]});}
            var Q76;
            {var subQ0=sQuery(id+"F2.wireOp",EDGE,"E27.top");var subQ1=sQuery(id+"F2.wireOp",EDGE,"E20.left");var subQ2=makeQuery(id+"F2.imprint","INTERSECT",VERTEX,{"derivedFrom":[subQ1,subQ0]});Q76=makeQuery(id+"F2.imprint","IMPRINT",FACE,{"disambiguationData":[TD([[makeQuery(id+"F2.imprint","IMPRINT",EDGE,{"disambiguationData":[TD([[subQ2,-1.0]])],"derivedFrom":subQ1}),-1.0]])]});}
            var Q77;
            {var subQ0=sQuery(id+"F2.wireOp",EDGE,"E22.bottom");var subQ1=sQuery(id+"F2.wireOp",EDGE,"E21.left");var subQ2=makeQuery(id+"F2.imprint","INTERSECT",VERTEX,{"derivedFrom":[subQ1,subQ0]});Q77=makeQuery(id+"F2.imprint","IMPRINT",FACE,{"disambiguationData":[TD([[makeQuery(id+"F2.imprint","IMPRINT",EDGE,{"disambiguationData":[TD([[subQ2,-1.0]])],"derivedFrom":subQ1}),1.0]])]});}
            var Q78;
            {var subQ0=sQuery(id+"F2.wireOp",EDGE,"E25.left");var subQ1=sQuery(id+"F2.wireOp",EDGE,"E22.bottom");var subQ2=makeQuery(id+"F2.imprint","INTERSECT",VERTEX,{"derivedFrom":[subQ1,subQ0]});Q78=makeQuery(id+"F2.imprint","IMPRINT",FACE,{"disambiguationData":[TD([[makeQuery(id+"F2.imprint","IMPRINT",EDGE,{"disambiguationData":[TD([[subQ2,-1.0]])],"derivedFrom":subQ1}),1.0]])]});}
            var Q79;
            {var subQ0=sQuery(id+"F2.wireOp",EDGE,"E28.top");var subQ1=sQuery(id+"F2.wireOp",EDGE,"E21.left");var subQ2=makeQuery(id+"F2.imprint","INTERSECT",VERTEX,{"derivedFrom":[subQ1,subQ0]});Q79=makeQuery(id+"F2.imprint","IMPRINT",FACE,{"disambiguationData":[TD([[makeQuery(id+"F2.imprint","IMPRINT",EDGE,{"disambiguationData":[TD([[subQ2,-1.0]])],"derivedFrom":subQ1}),-1.0]])]});}
            var Q80;
            {var subQ0=sQuery(id+"F2.wireOp",EDGE,"E28.bottom");var subQ1=sQuery(id+"F2.wireOp",EDGE,"E21.left");var subQ2=makeQuery(id+"F2.imprint","INTERSECT",VERTEX,{"derivedFrom":[subQ1,subQ0]});Q80=makeQuery(id+"F2.imprint","IMPRINT",FACE,{"disambiguationData":[TD([[makeQuery(id+"F2.imprint","IMPRINT",EDGE,{"disambiguationData":[TD([[subQ2,-1.0]])],"derivedFrom":subQ1}),-1.0]])]});}
            var Q81;
            {var subQ0=sQuery(id+"F2.wireOp",EDGE,"E28.top");var subQ1=sQuery(id+"F2.wireOp",EDGE,"E21.left");var subQ2=makeQuery(id+"F2.imprint","INTERSECT",VERTEX,{"derivedFrom":[subQ1,subQ0]});Q81=makeQuery(id+"F2.imprint","IMPRINT",FACE,{"disambiguationData":[TD([[makeQuery(id+"F2.imprint","IMPRINT",EDGE,{"disambiguationData":[TD([[subQ2,-1.0]])],"derivedFrom":subQ1}),1.0]])]});}
            var Q82;
            {var subQ0=sQuery(id+"F2.wireOp",EDGE,"E28.top");var subQ1=sQuery(id+"F2.wireOp",EDGE,"E20.right");var subQ2=makeQuery(id+"F2.imprint","INTERSECT",VERTEX,{"derivedFrom":[subQ1,subQ0]});Q82=makeQuery(id+"F2.imprint","IMPRINT",FACE,{"disambiguationData":[TD([[makeQuery(id+"F2.imprint","IMPRINT",EDGE,{"disambiguationData":[TD([[subQ2,-1.0]])],"derivedFrom":subQ1}),-1.0]])]});}
            var Q83;
            {var subQ0=sQuery(id+"F2.wireOp",EDGE,"E22.bottom");var subQ1=sQuery(id+"F2.wireOp",EDGE,"E20.right");var subQ2=makeQuery(id+"F2.imprint","INTERSECT",VERTEX,{"derivedFrom":[subQ1,subQ0]});Q83=makeQuery(id+"F2.imprint","IMPRINT",FACE,{"disambiguationData":[TD([[makeQuery(id+"F2.imprint","IMPRINT",EDGE,{"disambiguationData":[TD([[subQ2,-1.0]])],"derivedFrom":subQ1}),-1.0]])]});}
            var Q84;
            {var subQ0=sQuery(id+"F2.wireOp",EDGE,"E26.left");var subQ1=sQuery(id+"F2.wireOp",EDGE,"E22.bottom");var subQ2=makeQuery(id+"F2.imprint","INTERSECT",VERTEX,{"derivedFrom":[subQ1,subQ0]});Q84=makeQuery(id+"F2.imprint","IMPRINT",FACE,{"disambiguationData":[TD([[makeQuery(id+"F2.imprint","IMPRINT",EDGE,{"disambiguationData":[TD([[subQ2,-1.0]])],"derivedFrom":subQ1}),1.0]])]});}
            var Q85;
            {var subQ0=sQuery(id+"F2.wireOp",EDGE,"E28.top");var subQ1=sQuery(id+"F2.wireOp",EDGE,"E25.left");var subQ2=makeQuery(id+"F2.imprint","INTERSECT",VERTEX,{"derivedFrom":[subQ1,subQ0]});Q85=makeQuery(id+"F2.imprint","IMPRINT",FACE,{"disambiguationData":[TD([[makeQuery(id+"F2.imprint","IMPRINT",EDGE,{"disambiguationData":[TD([[subQ2,-1.0]])],"derivedFrom":subQ1}),-1.0]])]});}
            var Q86;
            {var subQ0=sQuery(id+"F2.wireOp",EDGE,"E28.top");var subQ1=sQuery(id+"F2.wireOp",EDGE,"E19.right");var subQ2=makeQuery(id+"F2.imprint","INTERSECT",VERTEX,{"derivedFrom":[subQ1,subQ0]});Q86=makeQuery(id+"F2.imprint","IMPRINT",FACE,{"disambiguationData":[TD([[makeQuery(id+"F2.imprint","IMPRINT",EDGE,{"disambiguationData":[TD([[subQ2,-1.0]])],"derivedFrom":subQ1}),-1.0]])]});}
            var Q87;
            {var subQ0=sQuery(id+"F2.wireOp",EDGE,"E28.top");var subQ1=sQuery(id+"F2.wireOp",EDGE,"E19.left");var subQ2=makeQuery(id+"F2.imprint","INTERSECT",VERTEX,{"derivedFrom":[subQ1,subQ0]});Q87=makeQuery(id+"F2.imprint","IMPRINT",FACE,{"disambiguationData":[TD([[makeQuery(id+"F2.imprint","IMPRINT",EDGE,{"disambiguationData":[TD([[subQ2,-1.0]])],"derivedFrom":subQ1}),-1.0]])]});}
            var Q88;
            {var subQ0=sQuery(id+"F2.wireOp",EDGE,"E28.bottom");var subQ1=sQuery(id+"F2.wireOp",EDGE,"E19.left");var subQ2=makeQuery(id+"F2.imprint","INTERSECT",VERTEX,{"derivedFrom":[subQ1,subQ0]});Q88=makeQuery(id+"F2.imprint","IMPRINT",FACE,{"disambiguationData":[TD([[makeQuery(id+"F2.imprint","IMPRINT",EDGE,{"disambiguationData":[TD([[subQ2,-1.0]])],"derivedFrom":subQ1}),-1.0]])]});}
            var Q89;
            {var subQ5=sQuery(id+"F2.wireOp",EDGE,"E26.top");Q89=makeQuery(id+"F2.imprint","IMPRINT",FACE,{"disambiguationData":[TD([[makeQuery(id+"F2.imprint","IMPRINT",EDGE,{"derivedFrom":subQ5}),-1.0]])]});}
            var Q90;
            {var subQ0=sQuery(id+"F2.wireOp",EDGE,"E24.bottom");var subQ1=sQuery(id+"F2.wireOp",EDGE,"E20.right");var subQ2=makeQuery(id+"F2.imprint","INTERSECT",VERTEX,{"derivedFrom":[subQ1,subQ0]});Q90=makeQuery(id+"F2.imprint","IMPRINT",FACE,{"disambiguationData":[TD([[makeQuery(id+"F2.imprint","IMPRINT",EDGE,{"disambiguationData":[TD([[subQ2,-1.0]])],"derivedFrom":subQ1}),-1.0]])]});}
            var Q91;
            {var subQ0=sQuery(id+"F2.wireOp",EDGE,"E26.left");var subQ1=sQuery(id+"F2.wireOp",EDGE,"E24.bottom");var subQ2=makeQuery(id+"F2.imprint","INTERSECT",VERTEX,{"derivedFrom":[subQ1,subQ0]});Q91=makeQuery(id+"F2.imprint","IMPRINT",FACE,{"disambiguationData":[TD([[makeQuery(id+"F2.imprint","IMPRINT",EDGE,{"disambiguationData":[TD([[subQ2,-1.0]])],"derivedFrom":subQ1}),-1.0]])]});}
            var Q92;
            {var subQ0=sQuery(id+"F2.wireOp",EDGE,"E26.left");var subQ1=sQuery(id+"F2.wireOp",EDGE,"E24.bottom");var subQ2=makeQuery(id+"F2.imprint","INTERSECT",VERTEX,{"derivedFrom":[subQ1,subQ0]});Q92=makeQuery(id+"F2.imprint","IMPRINT",FACE,{"disambiguationData":[TD([[makeQuery(id+"F2.imprint","IMPRINT",EDGE,{"disambiguationData":[TD([[subQ2,-1.0]])],"derivedFrom":subQ1}),1.0]])]});}
            var Q93;
            {var subQ0=sQuery(id+"F2.wireOp",EDGE,"E28.bottom");var subQ1=sQuery(id+"F2.wireOp",EDGE,"E20.left");var subQ2=makeQuery(id+"F2.imprint","INTERSECT",VERTEX,{"derivedFrom":[subQ1,subQ0]});Q93=makeQuery(id+"F2.imprint","IMPRINT",FACE,{"disambiguationData":[TD([[makeQuery(id+"F2.imprint","IMPRINT",EDGE,{"disambiguationData":[TD([[subQ2,-1.0]])],"derivedFrom":subQ1}),-1.0]])]});}
            var Q94;
            {var subQ0=sQuery(id+"F2.wireOp",EDGE,"E28.top");var subQ1=sQuery(id+"F2.wireOp",EDGE,"E20.left");var subQ2=makeQuery(id+"F2.imprint","INTERSECT",VERTEX,{"derivedFrom":[subQ1,subQ0]});Q94=makeQuery(id+"F2.imprint","IMPRINT",FACE,{"disambiguationData":[TD([[makeQuery(id+"F2.imprint","IMPRINT",EDGE,{"disambiguationData":[TD([[subQ2,-1.0]])],"derivedFrom":subQ1}),-1.0]])]});}
            var Q95;
            {var subQ5=sQuery(id+"F2.wireOp",EDGE,"E28.left");Q95=makeQuery(id+"F2.imprint","IMPRINT",FACE,{"disambiguationData":[TD([[makeQuery(id+"F2.imprint","IMPRINT",EDGE,{"derivedFrom":subQ5}),1.0]])]});}
            var Q96;
            {var subQ5=sQuery(id+"F2.wireOp",EDGE,"E28.right");Q96=makeQuery(id+"F2.imprint","IMPRINT",FACE,{"disambiguationData":[TD([[makeQuery(id+"F2.imprint","IMPRINT",EDGE,{"derivedFrom":subQ5}),-1.0]])]});}
            var Q97;
            {var subQ0=sQuery(id+"F2.wireOp",EDGE,"E24.bottom");var subQ1=sQuery(id+"F2.wireOp",EDGE,"E21.left");var subQ2=makeQuery(id+"F2.imprint","INTERSECT",VERTEX,{"derivedFrom":[subQ1,subQ0]});Q97=makeQuery(id+"F2.imprint","IMPRINT",FACE,{"disambiguationData":[TD([[makeQuery(id+"F2.imprint","IMPRINT",EDGE,{"disambiguationData":[TD([[subQ2,-1.0]])],"derivedFrom":subQ1}),1.0]])]});}
            var Q98;
            {var subQ5=sQuery(id+"F2.wireOp",EDGE,"E25.top");Q98=makeQuery(id+"F2.imprint","IMPRINT",FACE,{"disambiguationData":[TD([[makeQuery(id+"F2.imprint","IMPRINT",EDGE,{"derivedFrom":subQ5}),-1.0]])]});}
            var Q99;
            {var subQ0=sQuery(id+"F2.wireOp",EDGE,"E25.left");var subQ1=sQuery(id+"F2.wireOp",EDGE,"E24.bottom");var subQ2=makeQuery(id+"F2.imprint","INTERSECT",VERTEX,{"derivedFrom":[subQ1,subQ0]});Q99=makeQuery(id+"F2.imprint","IMPRINT",FACE,{"disambiguationData":[TD([[makeQuery(id+"F2.imprint","IMPRINT",EDGE,{"disambiguationData":[TD([[subQ2,-1.0]])],"derivedFrom":subQ1}),1.0]])]});}
            var Q100;
            {var subQ0=sQuery(id+"F2.wireOp",EDGE,"E25.left");var subQ1=sQuery(id+"F2.wireOp",EDGE,"E24.bottom");var subQ2=makeQuery(id+"F2.imprint","INTERSECT",VERTEX,{"derivedFrom":[subQ1,subQ0]});Q100=makeQuery(id+"F2.imprint","IMPRINT",FACE,{"disambiguationData":[TD([[makeQuery(id+"F2.imprint","IMPRINT",EDGE,{"disambiguationData":[TD([[subQ2,-1.0]])],"derivedFrom":subQ1}),-1.0]])]});}
            var Q101;
            {var subQ0=sQuery(id+"F2.wireOp",EDGE,"E27.top");var subQ1=sQuery(id+"F2.wireOp",EDGE,"E19.left");var subQ2=makeQuery(id+"F2.imprint","INTERSECT",VERTEX,{"derivedFrom":[subQ1,subQ0]});Q101=makeQuery(id+"F2.imprint","IMPRINT",FACE,{"disambiguationData":[TD([[makeQuery(id+"F2.imprint","IMPRINT",EDGE,{"disambiguationData":[TD([[subQ2,-1.0]])],"derivedFrom":subQ1}),-1.0]])]});}
            var Q102;
            {var subQ0=sQuery(id+"F2.wireOp",EDGE,"E26.left");var subQ1=sQuery(id+"F2.wireOp",EDGE,"E22.top");var subQ2=makeQuery(id+"F2.imprint","INTERSECT",VERTEX,{"derivedFrom":[subQ1,subQ0]});Q102=makeQuery(id+"F2.imprint","IMPRINT",FACE,{"disambiguationData":[TD([[makeQuery(id+"F2.imprint","IMPRINT",EDGE,{"disambiguationData":[TD([[subQ2,-1.0]])],"derivedFrom":subQ1}),1.0]])]});}
            var Q103;
            {var subQ0=sQuery(id+"F2.wireOp",EDGE,"E28.top");var subQ1=sQuery(id+"F2.wireOp",EDGE,"E19.left");var subQ2=makeQuery(id+"F2.imprint","INTERSECT",VERTEX,{"derivedFrom":[subQ1,subQ0]});Q103=makeQuery(id+"F2.imprint","IMPRINT",FACE,{"disambiguationData":[TD([[makeQuery(id+"F2.imprint","IMPRINT",EDGE,{"disambiguationData":[TD([[subQ2,-1.0]])],"derivedFrom":subQ1}),1.0]])]});}
            var Q104;
            {var subQ0=sQuery(id+"F2.wireOp",EDGE,"E28.top");var subQ1=sQuery(id+"F2.wireOp",EDGE,"E26.left");var subQ2=makeQuery(id+"F2.imprint","INTERSECT",VERTEX,{"derivedFrom":[subQ1,subQ0]});Q104=makeQuery(id+"F2.imprint","IMPRINT",FACE,{"disambiguationData":[TD([[makeQuery(id+"F2.imprint","IMPRINT",EDGE,{"disambiguationData":[TD([[subQ2,-1.0]])],"derivedFrom":subQ1}),-1.0]])]});}
            var Q105;
            {var subQ0=sQuery(id+"F2.wireOp",EDGE,"E25.left");var subQ1=sQuery(id+"F2.wireOp",EDGE,"E22.top");var subQ2=makeQuery(id+"F2.imprint","INTERSECT",VERTEX,{"derivedFrom":[subQ1,subQ0]});Q105=makeQuery(id+"F2.imprint","IMPRINT",FACE,{"disambiguationData":[TD([[makeQuery(id+"F2.imprint","IMPRINT",EDGE,{"disambiguationData":[TD([[subQ2,-1.0]])],"derivedFrom":subQ1}),1.0]])]});}
            var Q106;
            {var subQ0=sQuery(id+"F2.wireOp",EDGE,"E27.top");var subQ1=sQuery(id+"F2.wireOp",EDGE,"E19.right");var subQ2=makeQuery(id+"F2.imprint","INTERSECT",VERTEX,{"derivedFrom":[subQ1,subQ0]});Q106=makeQuery(id+"F2.imprint","IMPRINT",FACE,{"disambiguationData":[TD([[makeQuery(id+"F2.imprint","IMPRINT",EDGE,{"disambiguationData":[TD([[subQ2,-1.0]])],"derivedFrom":subQ1}),-1.0]])]});}
            var Q107;
            {var subQ0=sQuery(id+"F2.wireOp",EDGE,"E27.top");var subQ1=sQuery(id+"F2.wireOp",EDGE,"E26.left");var subQ2=makeQuery(id+"F2.imprint","INTERSECT",VERTEX,{"derivedFrom":[subQ1,subQ0]});Q107=makeQuery(id+"F2.imprint","IMPRINT",FACE,{"disambiguationData":[TD([[makeQuery(id+"F2.imprint","IMPRINT",EDGE,{"disambiguationData":[TD([[subQ2,-1.0]])],"derivedFrom":subQ1}),-1.0]])]});}
            var Q108;
            {var subQ0=sQuery(id+"F2.wireOp",EDGE,"E25.left");var subQ1=sQuery(id+"F2.wireOp",EDGE,"E23.bottom");var subQ2=makeQuery(id+"F2.imprint","INTERSECT",VERTEX,{"derivedFrom":[subQ1,subQ0]});Q108=makeQuery(id+"F2.imprint","IMPRINT",FACE,{"disambiguationData":[TD([[makeQuery(id+"F2.imprint","IMPRINT",EDGE,{"disambiguationData":[TD([[subQ2,-1.0]])],"derivedFrom":subQ1}),1.0]])]});}
            var Q109;
            Q109=makeQuery(id+"F2.imprint","IMPRINT",FACE,{"disambiguationData":[TD([[makeQuery(id+"F2.imprint","IMPRINT",EDGE,{"derivedFrom":makeQuery(id+"F1.opExtrude","CAP_EDGE",EDGE,{"disambiguationData":[OSD([sQuery(id+"F0.wireOp",EDGE,"E9")])],"isStart":true})}),1.0]])]});
            var Q110;
            Q110=makeQuery(id+"F2.imprint","IMPRINT",FACE,{"disambiguationData":[TD([[makeQuery(id+"F2.imprint","IMPRINT",EDGE,{"derivedFrom":makeQuery(id+"F1.opExtrude","CAP_EDGE",EDGE,{"disambiguationData":[OSD([sQuery(id+"F0.wireOp",EDGE,"E8")])],"isStart":true})}),1.0]])]});
            var Q111;
            Q111=makeQuery(id+"F2.imprint","IMPRINT",FACE,{"disambiguationData":[TD([[makeQuery(id+"F2.imprint","IMPRINT",EDGE,{"derivedFrom":makeQuery(id+"F1.opExtrude","CAP_EDGE",EDGE,{"disambiguationData":[OSD([sQuery(id+"F0.wireOp",EDGE,"E7")])],"isStart":true})}),1.0]])]});
            var Q112;
            Q112=makeQuery(id+"F2.imprint","IMPRINT",FACE,{"disambiguationData":[TD([[makeQuery(id+"F2.imprint","IMPRINT",EDGE,{"derivedFrom":makeQuery(id+"F1.opExtrude","CAP_EDGE",EDGE,{"disambiguationData":[OSD([sQuery(id+"F0.wireOp",EDGE,"E6")])],"isStart":true})}),1.0]])]});
            extrude(context, id + "F3", {"entities" : qUnion([Q0, Q1, Q2, Q3, Q4, Q5, Q6, Q7, Q8, Q9, Q10, Q11, Q12, Q13, Q14, Q15, Q16, Q17, Q18, Q19, Q20, Q21, Q22, Q23, Q24, Q25, Q26, Q27, Q28, Q29, Q30, Q31, Q32, Q33, Q34, Q35, Q36, Q37, Q38, Q39, Q40, Q41, Q42, Q43, Q44, Q45, Q46, Q47, Q48, Q49, Q50, Q51, Q52, Q53, Q54, Q55, Q56, Q57, Q58, Q59, Q60, Q61, Q62, Q63, Q64, Q65, Q66, Q67, Q68, Q69, Q70, Q71, Q72, Q73, Q74, Q75, Q76, Q77, Q78, Q79, Q80, Q81, Q82, Q83, Q84, Q85, Q86, Q87, Q88, Q89, Q90, Q91, Q92, Q93, Q94, Q95, Q96, Q97, Q98, Q99, Q100, Q101, Q102, Q103, Q104, Q105, Q106, Q107, Q108, Q109, Q110, Q111, Q112]), "operationType" : NewBodyOperationType.ADD, "depth" : 5 * mm, "offsetDistance" : 25 * mm});
        }
    });
